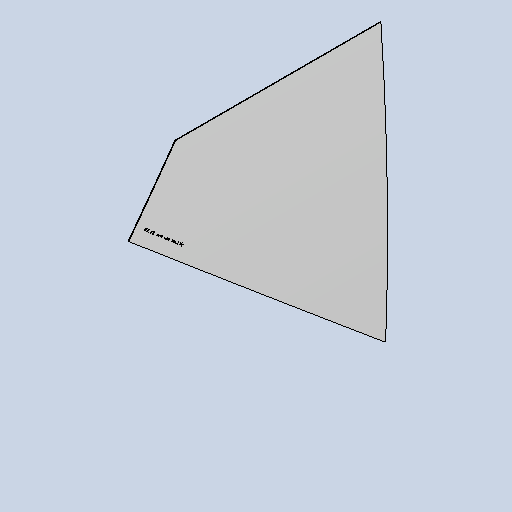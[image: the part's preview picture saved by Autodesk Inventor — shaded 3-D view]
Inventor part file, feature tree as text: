
AUTODESK INVENTOR PART (.ipt)
format: ipt  version: 2025 (Build 290162010, 162A)  size: 498,176 bytes
history: native  units: mm
features: sheet_metal_op x3, other x3, sketch x3, extrude x1, fillet x1, projected_geometry x1
ambient origin geometry x8: Origin, YZ Plane, XZ Plane, XY Plane, X Axis, Y Axis, Z Axis, Center Point
bodies: Body1 (feature_tree)
feature tree (12):
  sheet_metal_op  "Contour Flange2"
  extrude  "Extrusion2"  Depth=3.0mm
  fillet  "Fillet1"  Radius=1.5mm
  other  "Mark1"
  sketch  "Sketch1"  dims[d36=3.0mm d37=3.0mm d38=1.5mm]
  other  "Plate2"
  sheet_metal_op  "Bend2"
  sheet_metal_op  "Corner2"
  sketch  "Sketch2"  dims[d39=6.0mm]
  projected_geometry  "Projected Loop1"
  sketch  "Sketch3"  dims[d40=5.0mm d41=1250.0mm d42=5.0mm d43=3.0mm d44=12.0mm d45=3.0mm d46=5.0mm d54=1500.0mm d55=2700.0mm d58=2100.0mm d65=8.0mm d66=8.0mm d68=8.0mm d69=3.0mm d70=3.0mm d75=3.0mm d78=3.0mm d80=3.0mm d83=8.0mm d86=3.0mm d112=241.9mm d113=50.0mm d114=50.0mm d115=3.0mm d116=25.0mm d117=110.0mm d118=25.0mm d119=92.8mm d130=10.0mm d131=0.0mm d152=1286.0mm d153=290.0mm d173=345.609mm d174=3.0mm d176=12.0mm d177=200.0mm d178=50.0mm d179=50.0mm]
  other  "Definition1"
